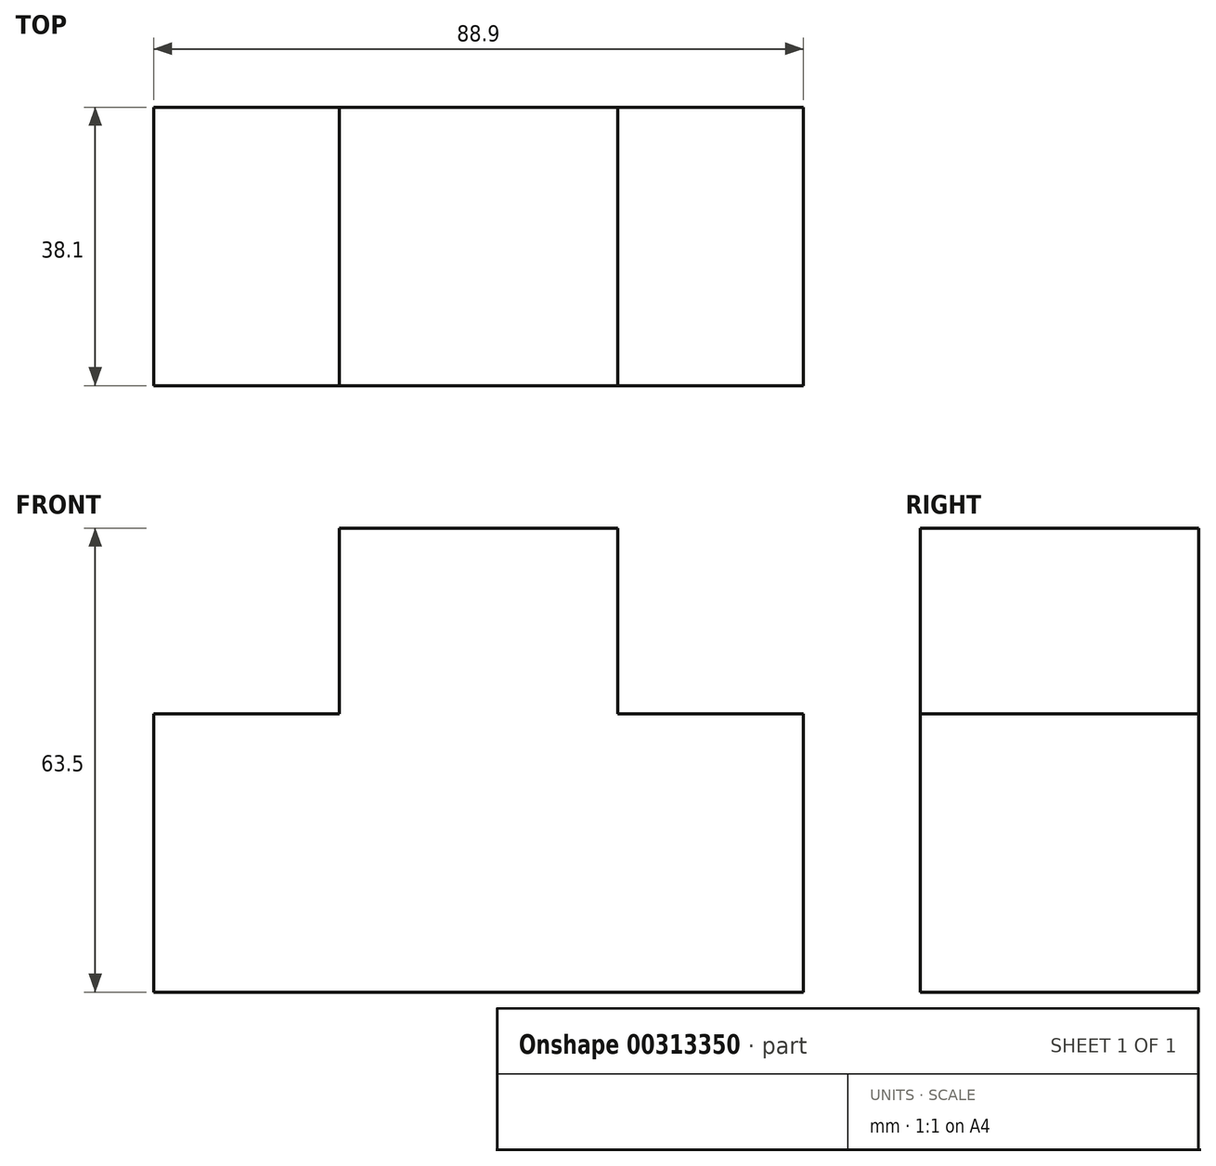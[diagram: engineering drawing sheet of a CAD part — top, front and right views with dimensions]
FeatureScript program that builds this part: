
annotation { "Feature Type Name" : "Feature", "Feature Type Description" : "" }
export const myFeature = defineFeature(function(context is Context, id is Id, definition is map)
    precondition{}
    {
        {
            var Q0;
            Q0=qCreatedBy(makeId("Front.planeOp"),FACE);
            var sketch = newSketch(context, id + "F0", { "sketchPlane" : qUnion([Q0])});
            skLineSegment(sketch, "E0", {"start": v(-41.14, -50.6) * mm, "end": v(47.76, -50.6) * mm});
            skLineSegment(sketch, "E1", {"start": v(47.76, -50.6) * mm, "end": v(47.76, -12.5) * mm});
            skLineSegment(sketch, "E2", {"start": v(47.76, -12.5) * mm, "end": v(22.36, -12.5) * mm});
            skLineSegment(sketch, "E3", {"start": v(22.36, -12.5) * mm, "end": v(22.36, 12.9) * mm});
            skLineSegment(sketch, "E4", {"start": v(22.36, 12.9) * mm, "end": v(-15.74, 12.9) * mm});
            skLineSegment(sketch, "E5", {"start": v(-15.74, 12.9) * mm, "end": v(-15.74, -12.5) * mm});
            skLineSegment(sketch, "E6", {"start": v(-15.74, -12.5) * mm, "end": v(-41.14, -12.5) * mm});
            skLineSegment(sketch, "E7", {"start": v(-41.14, -12.5) * mm, "end": v(-41.14, -50.6) * mm});
            skSolve(sketch);
        }
        {
            var Q0;
            Q0=makeQuery(id+"F0.imprint","IMPRINT",FACE,{"disambiguationData":[TD([[makeQuery(id+"F0.imprint","IMPRINT",EDGE,{"derivedFrom":sQuery(id+"F0.wireOp",EDGE,"E0")}),1.0]])]});
            extrude(context, id + "F1", {"entities" : qUnion([Q0]), "depth" : 38.1 * mm});
        }
    });
